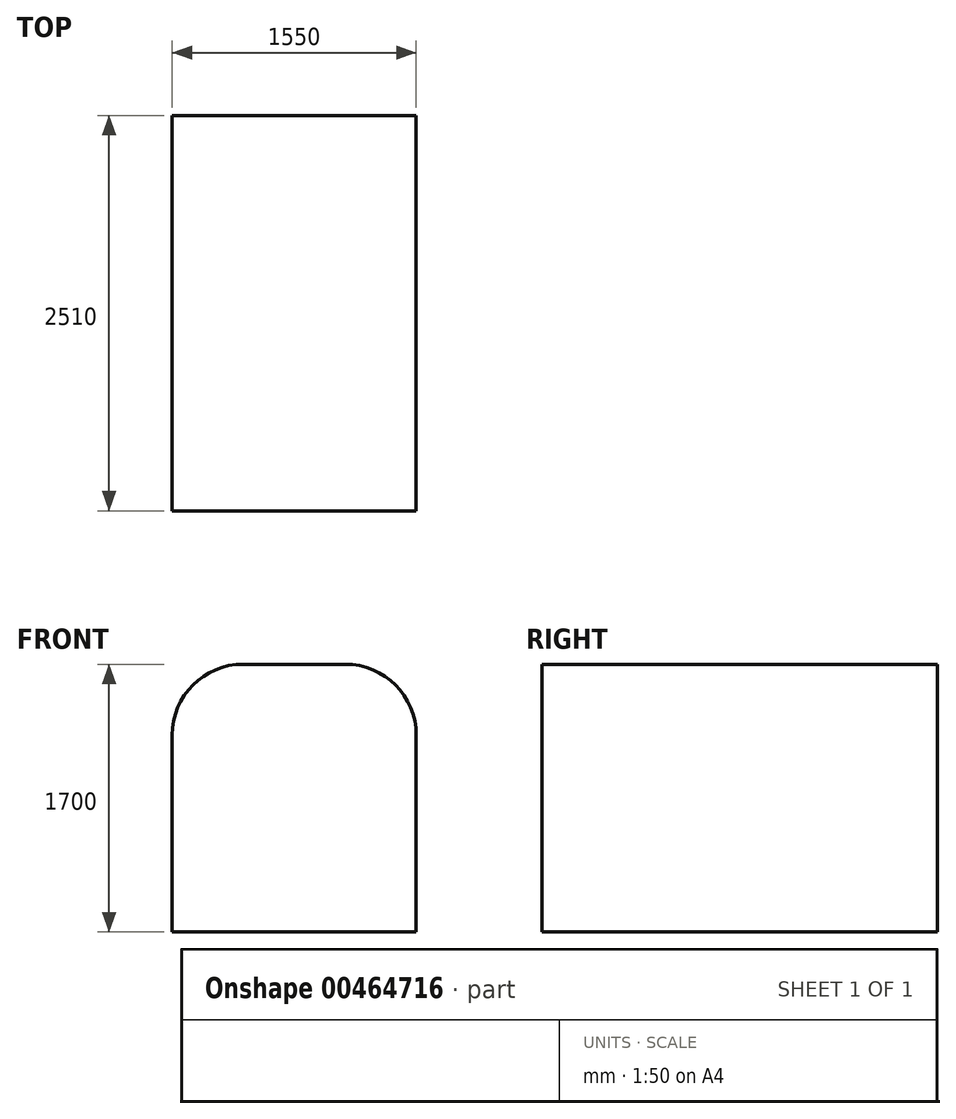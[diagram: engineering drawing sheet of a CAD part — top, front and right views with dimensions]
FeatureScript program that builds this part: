
annotation { "Feature Type Name" : "Feature", "Feature Type Description" : "" }
export const myFeature = defineFeature(function(context is Context, id is Id, definition is map)
    precondition{}
    {
        {
            var Q0;
            Q0=qCreatedBy(makeId("Front.planeOp"),FACE);
            var sketch = newSketch(context, id + "F0", { "sketchPlane" : qUnion([Q0])});
            skLineSegment(sketch, "E0", {"start": v(-775, 0) * mm, "end": v(775, 0) * mm});
            skLineSegment(sketch, "E1", {"start": v(0, 0) * mm, "end": v(0, 1700) * mm, "construction": true});
            skLineSegment(sketch, "E2", {"start": v(-325, 1700) * mm, "end": v(325, 1700) * mm});
            skArc(sketch, "E3", {"start": v(-325, 1700) * mm, "mid": v(-643.2, 1568.2) * mm, "end": v(-775, 1250) * mm});
            skLineSegment(sketch, "E4", {"start": v(-1625, 300) * mm, "end": v(-425, 300) * mm, "construction": true});
            skLineSegment(sketch, "E5", {"start": v(-1625, 300) * mm, "end": v(-1625, 633.56) * mm, "construction": true});
            skArc(sketch, "E6.MirrorCS", {"start": v(325, 1700) * mm, "mid": v(643.2, 1568.2) * mm, "end": v(775, 1250) * mm});
            skLineSegment(sketch, "E7", {"start": v(-775, 0) * mm, "end": v(-775, 1250) * mm});
            skLineSegment(sketch, "E8.MirrorCS", {"start": v(775, 0) * mm, "end": v(775, 1250) * mm});
            skCircle(sketch, "E9", {"center": v(-775, 1250) * mm, "radius": 1050 * mm, "construction": true});
            skCircle(sketch, "E10", {"center": v(-775, 300) * mm, "radius": 913.1 * mm, "construction": true});
            skSolve(sketch);
        }
        {
            var Q0;
            Q0=makeQuery(id+"F0.imprint","IMPRINT",FACE,{"disambiguationData":[TD([[makeQuery(id+"F0.imprint","IMPRINT",EDGE,{"derivedFrom":sQuery(id+"F0.wireOp",EDGE,"E0")}),1.0]])]});
            extrude(context, id + "F1", {"entities" : qUnion([Q0]), "depth" : 2510 * mm});
        }
    });
